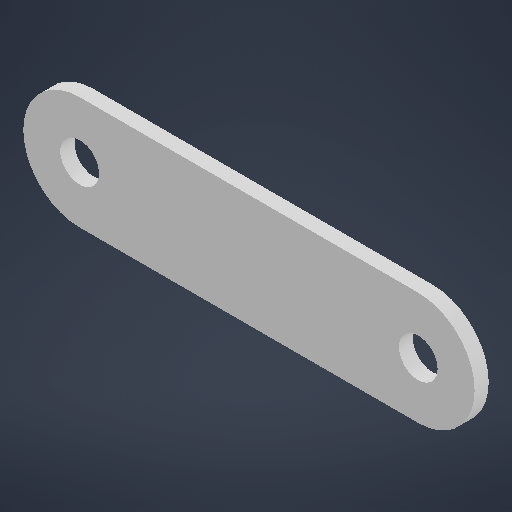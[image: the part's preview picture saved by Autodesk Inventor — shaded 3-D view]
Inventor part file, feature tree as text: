
AUTODESK INVENTOR PART (.ipt)
format: ipt  version: 2025.2 (Build 292293000, 293)  size: 174,080 bytes
history: native  units: in
note: dims shown in document units (in); Inventor stores cm internally (conversion verified against a paired STEP export)
features: extrude x1, sketch x1
ambient origin geometry x8: Origin, YZ Plane, XZ Plane, XY Plane, X Axis, Y Axis, Z Axis, Center Point
bodies: Solid1 (feature_tree)
feature tree (2):
  extrude  "Extrusion1"  Depth=0.0625in
  sketch  "Sketch1"  dims[d0=0.172in d2=0.172in d5=0.0625in d6=0.0in]
